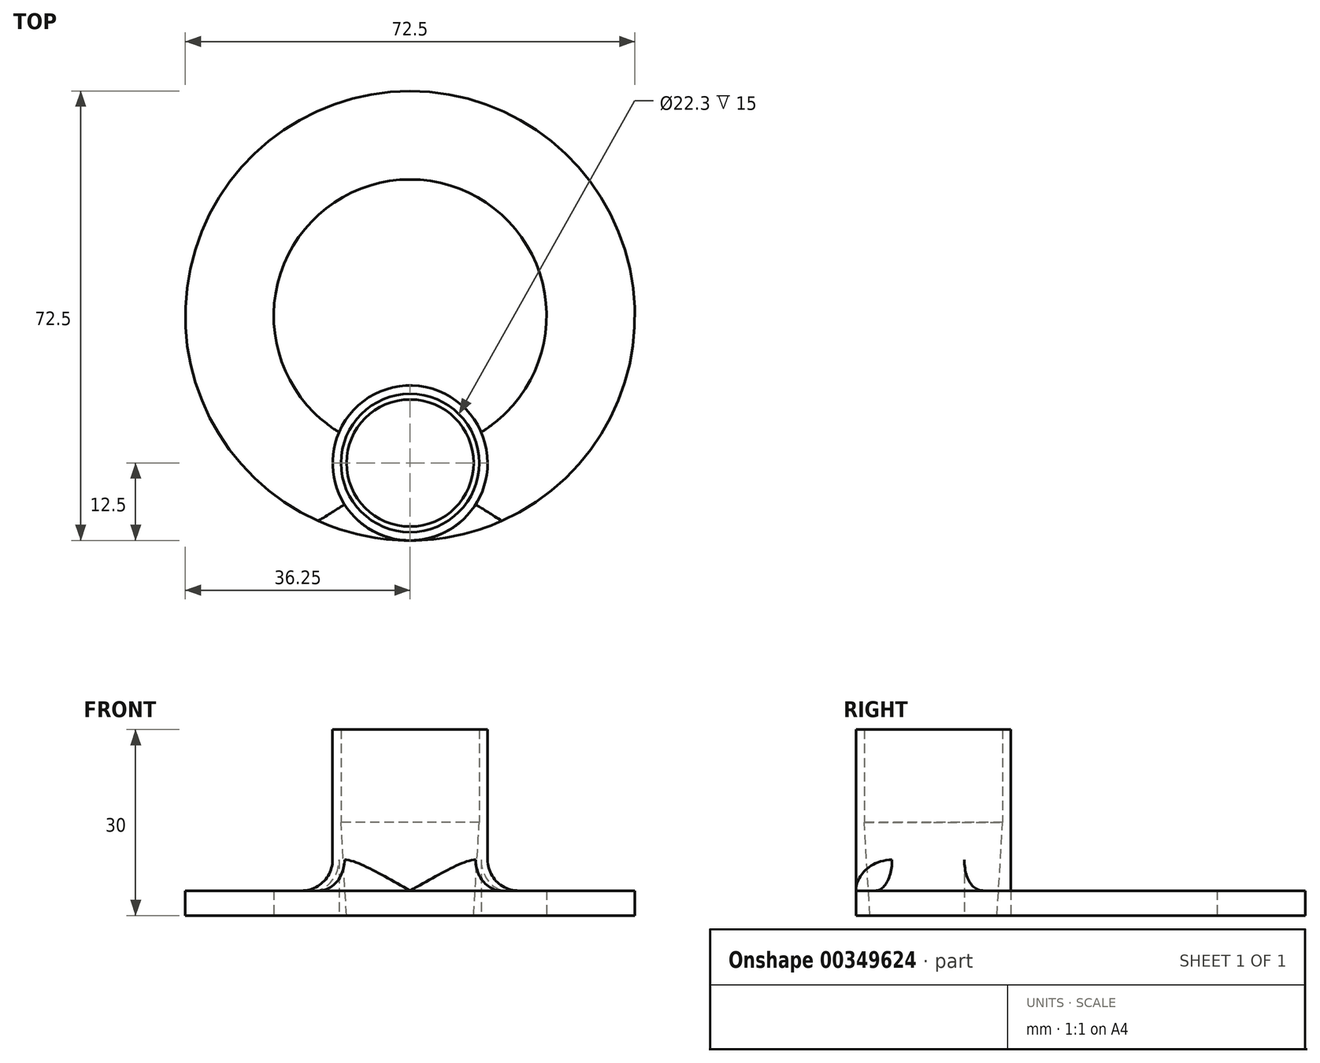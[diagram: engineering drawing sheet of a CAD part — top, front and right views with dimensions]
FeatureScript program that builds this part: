
annotation { "Feature Type Name" : "Feature", "Feature Type Description" : "" }
export const myFeature = defineFeature(function(context is Context, id is Id, definition is map)
    precondition{}
    {
        {
            var Q0;
            Q0=qCreatedBy(makeId("Top.planeOp"),FACE);
            var sketch = newSketch(context, id + "F0", { "sketchPlane" : qUnion([Q0])});
            skCircle(sketch, "E0", {"center": v(0, 0) * mm, "radius": 36.25 * mm});
            skCircle(sketch, "E1", {"center": v(0, 0) * mm, "radius": 22 * mm});
            skCircle(sketch, "E2", {"center": v(0, -23.75) * mm, "radius": 12.5 * mm});
            skCircle(sketch, "E3", {"center": v(0, -23.75) * mm, "radius": 10.25 * mm});
            skSolve(sketch);
        }
        {
            var Q0;
            Q0=makeQuery(id+"F0.imprint","IMPRINT",FACE,{"disambiguationData":[TD([[makeQuery(id+"F0.imprint","IMPRINT",EDGE,{"derivedFrom":sQuery(id+"F0.wireOp",EDGE,"E0")}),1.0]])]});
            var Q1;
            {var subQ0=sQuery(id+"F0.wireOp",EDGE,"E2");var subQ1=sQuery(id+"F0.wireOp",EDGE,"E1");var subQ2=makeQuery(id+"F0.imprint","INTERSECT",VERTEX,{"disambiguationData":[OD(0.0)],"derivedFrom":[subQ1,subQ0]});Q1=makeQuery(id+"F0.imprint","IMPRINT",FACE,{"disambiguationData":[TD([[makeQuery(id+"F0.imprint","IMPRINT",EDGE,{"disambiguationData":[TD([[subQ2,-1.0]])],"derivedFrom":subQ1}),-1.0]])]});}
            extrude(context, id + "F1", {"entities" : qUnion([Q0, Q1]), "depth" : 4 * mm});
        }
        {
            var Q0;
            {var subQ0=sQuery(id+"F0.wireOp",EDGE,"E2");var subQ1=sQuery(id+"F0.wireOp",EDGE,"E1");var subQ2=makeQuery(id+"F0.imprint","INTERSECT",VERTEX,{"disambiguationData":[OD(0.0)],"derivedFrom":[subQ1,subQ0]});Q0=makeQuery(id+"F0.imprint","IMPRINT",FACE,{"disambiguationData":[TD([[makeQuery(id+"F0.imprint","IMPRINT",EDGE,{"disambiguationData":[TD([[subQ2,-1.0]])],"derivedFrom":subQ1}),1.0]])]});}
            var Q1;
            {var subQ0=sQuery(id+"F0.wireOp",EDGE,"E2");var subQ1=sQuery(id+"F0.wireOp",EDGE,"E1");var subQ2=makeQuery(id+"F0.imprint","INTERSECT",VERTEX,{"disambiguationData":[OD(0.0)],"derivedFrom":[subQ1,subQ0]});Q1=makeQuery(id+"F0.imprint","IMPRINT",FACE,{"disambiguationData":[TD([[makeQuery(id+"F0.imprint","IMPRINT",EDGE,{"disambiguationData":[TD([[subQ2,-1.0]])],"derivedFrom":subQ1}),-1.0]])]});}
            extrude(context, id + "F2", {"entities" : qUnion([Q0, Q1]), "operationType" : NewBodyOperationType.ADD, "depth" : 15 * mm});
        }
        {
            var Q0;
            Q0=makeQuery(id+"F2.opExtrude","CAP_FACE",FACE,{"disambiguationData":[OSD([sQuery(id+"F0.wireOp",EDGE,"E2")])],"isStart":false});
            var sketch = newSketch(context, id + "F3", { "sketchPlane" : qUnion([Q0])});
            skCircle(sketch, "E4", {"center": v(0, -23.75) * mm, "radius": 11.15 * mm});
            skSolve(sketch);
        }
        {
            var Q0;
            Q0=makeQuery(id+"F3.imprint","IMPRINT",FACE,{"disambiguationData":[TD([[makeQuery(id+"F3.imprint","IMPRINT",EDGE,{"derivedFrom":sQuery(id+"F3.wireOp",EDGE,"E4")}),1.0]])]});
            var sketch = newSketch(context, id + "F4", { "sketchPlane" : qUnion([Q0])});
            skCircle(sketch, "E5.0", {"center": v(0, -23.75) * mm, "radius": 11.15 * mm});
            skSolve(sketch);
        }
        {
            var Q0;
            Q0=qCreatedBy(makeId("Top.planeOp"),FACE);
            var sketch = newSketch(context, id + "F5", { "sketchPlane" : qUnion([Q0])});
            skCircle(sketch, "E6.0", {"center": v(0, -23.75) * mm, "radius": 10.25 * mm});
            skSolve(sketch);
        }
        {
            var Q1;
            Q1 = qSketchRegion(id + "F4", true);
            var Q2;
            Q2 = qSketchRegion(id + "F5", true);
            loft(context, id + "F6", {"operationType" : NewBodyOperationType.REMOVE, "sheetProfilesArray" : [{ "sheetProfileEntities" : qUnion([Q1]) }, { "sheetProfileEntities" : qUnion([Q2]) }]});
        }
        {
            var Q0;
            Q0=qCreatedBy(makeId("Front.planeOp"),FACE);
            var sketch = newSketch(context, id + "F7", { "sketchPlane" : qUnion([Q0])});
            skLineSegment(sketch, "E7", {"start": v(0, 34.54) * mm, "end": v(0, -11.33) * mm, "construction": true});
            skSolve(sketch);
        }
        {
            var Q0;
            Q0=makeQuery(id+"F2.opExtrude","CAP_FACE",FACE,{"disambiguationData":[OSD([sQuery(id+"F0.wireOp",EDGE,"E2"),sQuery(id+"F0.wireOp",EDGE,"E3")])],"isStart":false});
            extrude(context, id + "F8", {"entities" : qUnion([Q0]), "operationType" : NewBodyOperationType.ADD, "depth" : 15 * mm});
        }
        {
            var Q0;
            Q0=makeQuery(id+"F2.boolean.opBoolean","INTERSECT",EDGE,{"disambiguationData":[OD(0.0)],"derivedFrom":[makeQuery(id+"F1.opExtrude","CAP_FACE",FACE,{"disambiguationData":[OSD([sQuery(id+"F0.wireOp",EDGE,"E0"),sQuery(id+"F0.wireOp",EDGE,"E1"),sQuery(id+"F0.wireOp",EDGE,"E3")])],"isStart":false}),makeQuery(id+"F2.opExtrude","SWEPT_FACE",FACE,{"disambiguationData":[OSD([sQuery(id+"F0.wireOp",EDGE,"E2")])]})]});
            fillet(context, id + "F9", {"entities" : qUnion([Q0]), "radius" : 5 * mm, "tangentPropagation" : true, "allowEdgeOverflow" : false});
        }
    });
